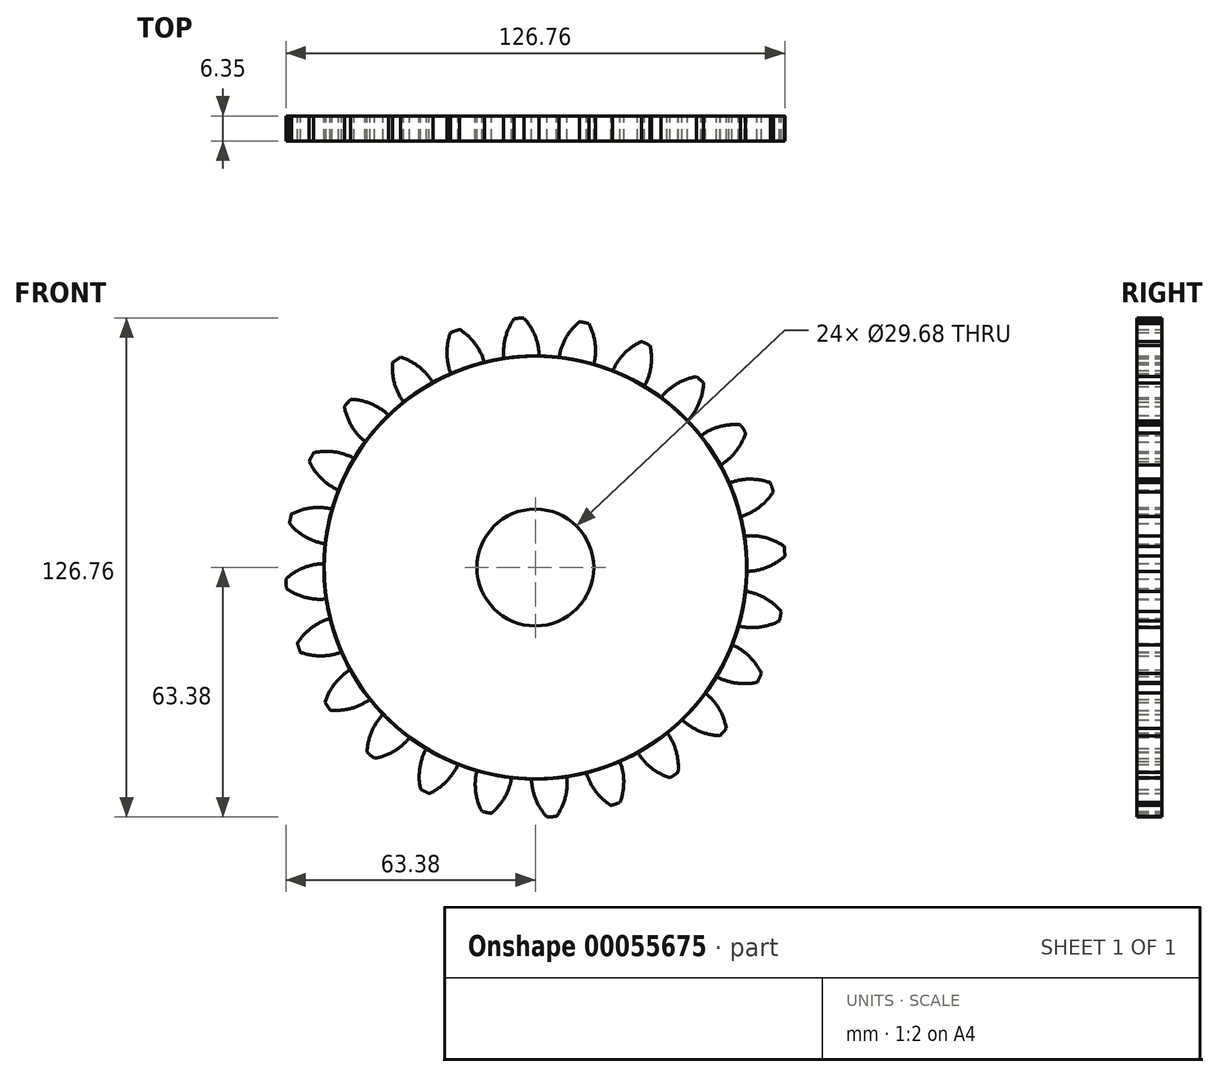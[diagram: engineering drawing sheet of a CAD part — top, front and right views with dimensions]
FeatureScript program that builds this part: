
annotation { "Feature Type Name" : "Feature", "Feature Type Description" : "" }
export const myFeature = defineFeature(function(context is Context, id is Id, definition is map)
    precondition{}
    {
        {
            var Q0;
            Q0=qCreatedBy(makeId("Front.planeOp"),FACE);
            var sketch = newSketch(context, id + "F0", { "sketchPlane" : qUnion([Q0])});
            skCircle(sketch, "E0", {"center": v(0, 0) * mm, "radius": 53.72 * mm});
            skCircle(sketch, "E1", {"center": v(0, 0) * mm, "radius": 58.67 * mm, "construction": true});
            skCircle(sketch, "E2", {"center": v(0, 0) * mm, "radius": 63.5 * mm, "construction": true});
            skLineSegment(sketch, "E3", {"start": v(0, 0) * mm, "end": v(0, 86.14) * mm, "construction": true});
            skLineSegment(sketch, "E4", {"start": v(0, 0) * mm, "end": v(-5.63, 85.93) * mm, "construction": true});
            skLineSegment(sketch, "E5", {"start": v(0, 58.67) * mm, "end": v(-87.75, 58.67) * mm, "construction": true});
            skLineSegment(sketch, "E6", {"start": v(0, 58.67) * mm, "end": v(-93.27, 24.72) * mm, "construction": true});
            skCircle(sketch, "E7", {"center": v(0, 58.67) * mm, "radius": 14.6 * mm, "construction": true});
            skCircle(sketch, "E8", {"center": v(0, 0) * mm, "radius": 55.14 * mm, "construction": true});
            skCircle(sketch, "E9", {"center": v(-13.62, 53.43) * mm, "radius": 14.6 * mm, "construction": true});
            skArc(sketch, "E10", {"start": v(0, 58.67) * mm, "mid": v(-1.24, 61.16) * mm, "end": v(-2.93, 63.38) * mm});
            skArc(sketch, "E11", {"start": v(0.99, 53.71) * mm, "mid": v(0.7, 56.24) * mm, "end": v(0, 58.67) * mm});
            skArc(sketch, "E12.MirrorCS", {"start": v(-7.66, 58.17) * mm, "mid": v(-6.75, 60.8) * mm, "end": v(-5.37, 63.22) * mm});
            skArc(sketch, "E13.MirrorCS", {"start": v(-7.99, 53.12) * mm, "mid": v(-8.04, 55.66) * mm, "end": v(-7.66, 58.17) * mm});
            skArc(sketch, "E14", {"start": v(-2.93, 63.38) * mm, "mid": v(-4.15, 63.33) * mm, "end": v(-5.37, 63.22) * mm});
            skCircle(sketch, "E15", {"center": v(0, 0) * mm, "radius": 14.84 * mm});
            skSolve(sketch);
        }
        {
            var Q0;
            {var subQ0=sQuery(id+"F0.wireOp",EDGE,"E0");var subQ1=makeQuery(id+"F0.imprint","INTERSECT",VERTEX,{"derivedFrom":[subQ0,sQuery(id+"F0.wireOp",EDGE,"E11")]});Q0=makeQuery(id+"F0.imprint","IMPRINT",FACE,{"disambiguationData":[TD([[makeQuery(id+"F0.imprint","IMPRINT",EDGE,{"disambiguationData":[TD([[subQ1,-1.0]])],"derivedFrom":subQ0}),1.0]])]});}
            var Q1;
            Q1=makeQuery(id+"F0.imprint","IMPRINT",FACE,{"disambiguationData":[TD([[makeQuery(id+"F0.imprint","IMPRINT",EDGE,{"derivedFrom":sQuery(id+"F0.wireOp",EDGE,"E10")}),1.0]])]});
            extrude(context, id + "F1", {"entities" : qUnion([Q0, Q1]), "depth" : 6.35 * mm});
        }
        {
            var Q0;
            Q0=makeQuery(id+"F1.opExtrude","SWEPT_BODY",BODY,{"disambiguationData":[OSD([sQuery(id+"F0.wireOp",EDGE,"E0"),sQuery(id+"F0.wireOp",EDGE,"E10"),sQuery(id+"F0.wireOp",EDGE,"E11"),sQuery(id+"F0.wireOp",EDGE,"E12.MirrorCS"),sQuery(id+"F0.wireOp",EDGE,"E13.MirrorCS"),sQuery(id+"F0.wireOp",EDGE,"E14")])]});
            var Q1;
            Q1=makeQuery(id+"F1.opExtrude","SWEPT_FACE",FACE,{"disambiguationData":[OSD([sQuery(id+"F0.wireOp",EDGE,"E0")])]});
            circularPattern(context, id + "F2", {"entities" : qUnion([Q0]), "axis" : qUnion([Q1]), "angle" : 15 * degree, "instanceCount" : 24});
        }
    });
